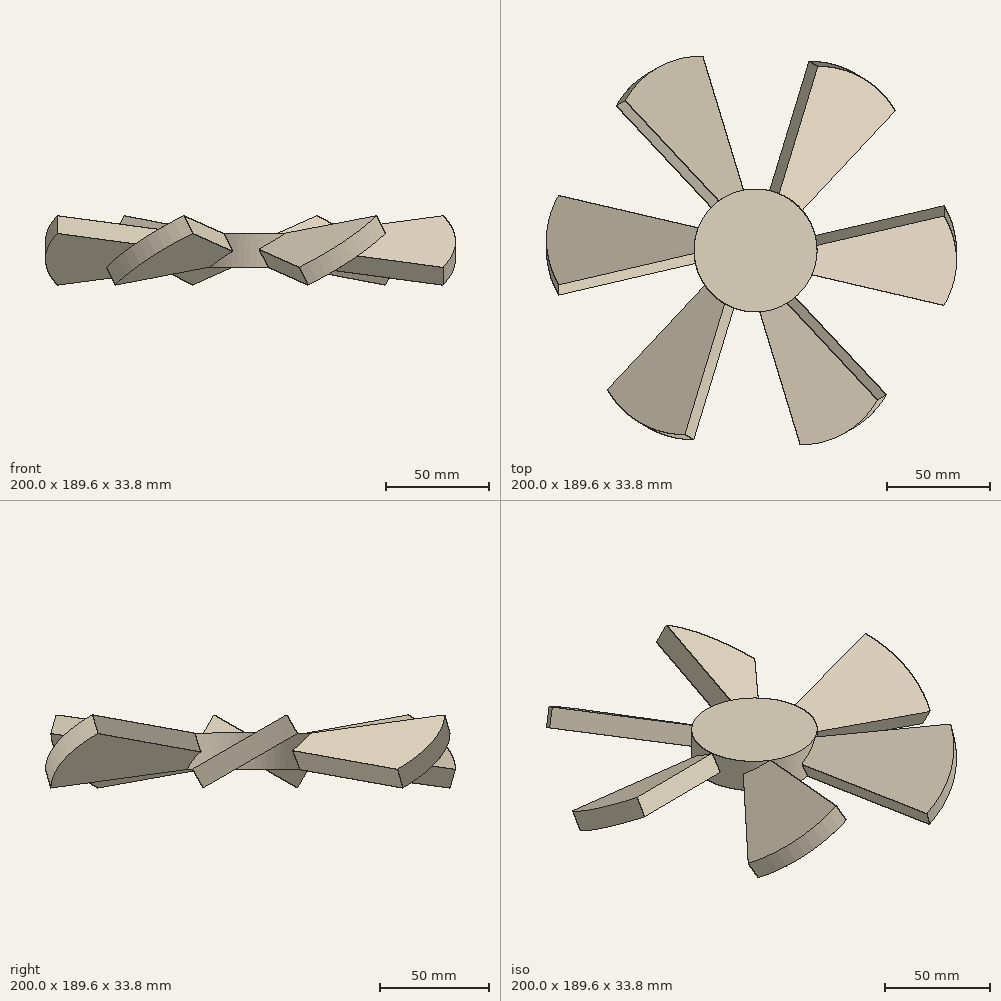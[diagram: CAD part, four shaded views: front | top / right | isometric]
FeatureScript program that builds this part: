
annotation { "Feature Type Name" : "Feature", "Feature Type Description" : "" }
export const myFeature = defineFeature(function(context is Context, id is Id, definition is map)
    precondition{}
    {
        {
            var Q0;
            Q0=qCreatedBy(makeId("Top.planeOp"),FACE);
            var sketch = newSketch(context, id + "F0", { "sketchPlane" : qUnion([Q0])});
            skLineSegment(sketch, "E0", {"start": v(0, 0) * mm, "end": v(94, 25.19) * mm});
            skLineSegment(sketch, "E1", {"start": v(0, 0) * mm, "end": v(94, -25.19) * mm});
            skArc(sketch, "E2", {"start": v(94, -25.19) * mm, "mid": v(100, 0) * mm, "end": v(94, 25.19) * mm});
            skSolve(sketch);
        }
        {
            var Q0;
            Q0=makeQuery(id+"F0.imprint","IMPRINT",FACE,{"disambiguationData":[TD([[makeQuery(id+"F0.imprint","IMPRINT",EDGE,{"derivedFrom":sQuery(id+"F0.wireOp",EDGE,"E0")}),-1.0]])]});
            extrude(context, id + "F1", {"entities" : qUnion([Q0]), "depth" : 5 * mm, "hasSecondDirection" : true, "secondDirectionOppositeDirection" : true, "secondDirectionDepth" : 5 * mm});
        }
        {
            var Q0;
            Q0=qCreatedBy(makeId("Right.planeOp"),FACE);
            var sketch = newSketch(context, id + "F2", { "sketchPlane" : qUnion([Q0])});
            skLineSegment(sketch, "E3", {"start": v(0, 0) * mm, "end": v(0, 134.87) * mm, "construction": true});
            skSolve(sketch);
        }
        {
            var Q0;
            Q0=makeQuery(id+"F1.opExtrude","CAP_FACE",FACE,{"disambiguationData":[OSD([sQuery(id+"F0.wireOp",EDGE,"E0"),sQuery(id+"F0.wireOp",EDGE,"E1"),sQuery(id+"F0.wireOp",EDGE,"E2")])],"isStart":true});
            var sketch = newSketch(context, id + "F3", { "sketchPlane" : qUnion([Q0])});
            skLineSegment(sketch, "E4", {"start": v(0, 0) * mm, "end": v(116.46, 0) * mm, "construction": true});
            skSolve(sketch);
        }
        {
            var Q0;
            Q0=makeQuery(id+"F1.opExtrude","SWEPT_BODY",BODY,{"disambiguationData":[OSD([sQuery(id+"F0.wireOp",EDGE,"E0"),sQuery(id+"F0.wireOp",EDGE,"E1"),sQuery(id+"F0.wireOp",EDGE,"E2")])]});
            var Q1;
            Q1=sQuery(id+"F3.wireOp",EDGE,"E4");
            transform(context, id + "F4", {"entities" : qUnion([Q0]), "transformType" : TransformType.ROTATION, "transformAxis" : qUnion([Q1]), "angle" : 30 * degree, "makeCopy" : false});
        }
        {
            var Q0;
            Q0=makeQuery(id+"F1.opExtrude","SWEPT_BODY",BODY,{"disambiguationData":[OSD([sQuery(id+"F0.wireOp",EDGE,"E0"),sQuery(id+"F0.wireOp",EDGE,"E1"),sQuery(id+"F0.wireOp",EDGE,"E2")])]});
            var Q1;
            Q1=sQuery(id+"F2.wireOp",EDGE,"E3");
            circularPattern(context, id + "F5", {"entities" : qUnion([Q0]), "axis" : qUnion([Q1]), "angle" : 360 * degree, "instanceCount" : 6, "equalSpace" : true});
        }
        {
            var Q0;
            Q0=qCreatedBy(makeId("Top.planeOp"),FACE);
            var sketch = newSketch(context, id + "F6", { "sketchPlane" : qUnion([Q0])});
            skCircle(sketch, "E5", {"center": v(2, 0) * mm, "radius": 30 * mm});
            skSolve(sketch);
        }
        {
            var Q0;
            Q0 = qSketchRegion(id + "F6", true);
            extrude(context, id + "F7", {"entities" : qUnion([Q0]), "depth" : 10 * mm, "hasSecondDirection" : true, "secondDirectionOppositeDirection" : true, "secondDirectionDepth" : 10 * mm});
        }
        {
            var Q0;
            Q0=makeQuery(id+"F5.opPattern","COPY",BODY,{"derivedFrom":makeQuery(id+"F1.opExtrude","SWEPT_BODY",BODY,{"disambiguationData":[OSD([sQuery(id+"F0.wireOp",EDGE,"E0"),sQuery(id+"F0.wireOp",EDGE,"E1"),sQuery(id+"F0.wireOp",EDGE,"E2")])]}),"instanceName":"3"});
            var Q1;
            Q1=makeQuery(id+"F5.opPattern","COPY",BODY,{"derivedFrom":makeQuery(id+"F1.opExtrude","SWEPT_BODY",BODY,{"disambiguationData":[OSD([sQuery(id+"F0.wireOp",EDGE,"E0"),sQuery(id+"F0.wireOp",EDGE,"E1"),sQuery(id+"F0.wireOp",EDGE,"E2")])]}),"instanceName":"2"});
            var Q2;
            Q2=makeQuery(id+"F5.opPattern","COPY",BODY,{"derivedFrom":makeQuery(id+"F1.opExtrude","SWEPT_BODY",BODY,{"disambiguationData":[OSD([sQuery(id+"F0.wireOp",EDGE,"E0"),sQuery(id+"F0.wireOp",EDGE,"E1"),sQuery(id+"F0.wireOp",EDGE,"E2")])]}),"instanceName":"1"});
            var Q3;
            Q3=makeQuery(id+"F1.opExtrude","SWEPT_BODY",BODY,{"disambiguationData":[OSD([sQuery(id+"F0.wireOp",EDGE,"E0"),sQuery(id+"F0.wireOp",EDGE,"E1"),sQuery(id+"F0.wireOp",EDGE,"E2")])]});
            var Q4;
            Q4=makeQuery(id+"F5.opPattern","COPY",BODY,{"derivedFrom":makeQuery(id+"F1.opExtrude","SWEPT_BODY",BODY,{"disambiguationData":[OSD([sQuery(id+"F0.wireOp",EDGE,"E0"),sQuery(id+"F0.wireOp",EDGE,"E1"),sQuery(id+"F0.wireOp",EDGE,"E2")])]}),"instanceName":"5"});
            var Q5;
            Q5=makeQuery(id+"F5.opPattern","COPY",BODY,{"derivedFrom":makeQuery(id+"F1.opExtrude","SWEPT_BODY",BODY,{"disambiguationData":[OSD([sQuery(id+"F0.wireOp",EDGE,"E0"),sQuery(id+"F0.wireOp",EDGE,"E1"),sQuery(id+"F0.wireOp",EDGE,"E2")])]}),"instanceName":"4"});
            var Q6;
            Q6=makeQuery(id+"F7.opExtrude","SWEPT_BODY",BODY,{"disambiguationData":[OSD([sQuery(id+"F6.wireOp",EDGE,"E5")])]});
            booleanBodies(context, id + "F8", {"operationType" : BooleanOperationType.UNION, "tools" : qUnion([Q0, Q1, Q2, Q3, Q4, Q5, Q6])});
        }
        {
            var Q0;
            {var subQ0=sQuery(id+"F0.wireOp",EDGE,"E0");Q0=makeQuery(id+"F8.opBoolean","INTERSECT",VERTEX,{"derivedFrom":[makeQuery(id+"F5.opPattern","COPY",FACE,{"derivedFrom":makeQuery(id+"F1.opExtrude","SWEPT_FACE",FACE,{"disambiguationData":[OSD([subQ0])]}),"instanceName":"4"}),makeQuery(id+"F5.opPattern","COPY",FACE,{"derivedFrom":makeQuery(id+"F1.opExtrude","CAP_FACE",FACE,{"disambiguationData":[OSD([subQ0,sQuery(id+"F0.wireOp",EDGE,"E1"),sQuery(id+"F0.wireOp",EDGE,"E2")])],"isStart":false}),"instanceName":"4"}),makeQuery(id+"F7.opExtrude","SWEPT_FACE",FACE,{"disambiguationData":[OSD([sQuery(id+"F6.wireOp",EDGE,"E5")])]})]});}
            var Q1;
            {var subQ0=sQuery(id+"F0.wireOp",EDGE,"E0");Q1=makeQuery(id+"F8.opBoolean","INTERSECT",VERTEX,{"derivedFrom":[makeQuery(id+"F1.opExtrude","SWEPT_FACE",FACE,{"disambiguationData":[OSD([subQ0])]}),makeQuery(id+"F1.opExtrude","CAP_FACE",FACE,{"disambiguationData":[OSD([subQ0,sQuery(id+"F0.wireOp",EDGE,"E1"),sQuery(id+"F0.wireOp",EDGE,"E2")])],"isStart":false}),makeQuery(id+"F7.opExtrude","SWEPT_FACE",FACE,{"disambiguationData":[OSD([sQuery(id+"F6.wireOp",EDGE,"E5")])]})]});}
            var Q2;
            {var subQ0=sQuery(id+"F0.wireOp",EDGE,"E0");Q2=makeQuery(id+"F8.opBoolean","INTERSECT",VERTEX,{"derivedFrom":[makeQuery(id+"F5.opPattern","COPY",FACE,{"derivedFrom":makeQuery(id+"F1.opExtrude","SWEPT_FACE",FACE,{"disambiguationData":[OSD([subQ0])]}),"instanceName":"2"}),makeQuery(id+"F5.opPattern","COPY",FACE,{"derivedFrom":makeQuery(id+"F1.opExtrude","CAP_FACE",FACE,{"disambiguationData":[OSD([subQ0,sQuery(id+"F0.wireOp",EDGE,"E1"),sQuery(id+"F0.wireOp",EDGE,"E2")])],"isStart":false}),"instanceName":"2"}),makeQuery(id+"F7.opExtrude","SWEPT_FACE",FACE,{"disambiguationData":[OSD([sQuery(id+"F6.wireOp",EDGE,"E5")])]})]});}
            cPlane(context, id + "F9", {"entities" : qUnion([Q0, Q1, Q2]), "cplaneType" : CPlaneType.THREE_POINT, "offset" : 25 * mm, "width" : 150 * mm, "height" : 150 * mm});
        }
        {
            var Q0;
            Q0=makeQuery(id+"F7.opExtrude","CAP_FACE",FACE,{"disambiguationData":[OSD([sQuery(id+"F6.wireOp",EDGE,"E5")])],"isStart":false});
            var Q1;
            Q1=qCreatedBy(id+"F9.planeOp",FACE);
            extrude(context, id + "F10", {"entities" : qUnion([Q0]), "operationType" : NewBodyOperationType.REMOVE, "endBound" : BoundingType.UP_TO_SURFACE, "oppositeDirection" : true, "endBoundEntityFace" : qUnion([Q1]), "depth" : 25 * mm});
        }
        {
            var Q0;
            {var subQ0=sQuery(id+"F0.wireOp",EDGE,"E1");Q0=makeQuery(id+"F8.opBoolean","INTERSECT",VERTEX,{"derivedFrom":[makeQuery(id+"F1.opExtrude","CAP_FACE",FACE,{"disambiguationData":[OSD([sQuery(id+"F0.wireOp",EDGE,"E0"),subQ0,sQuery(id+"F0.wireOp",EDGE,"E2")])],"isStart":true}),makeQuery(id+"F1.opExtrude","SWEPT_FACE",FACE,{"disambiguationData":[OSD([subQ0])]}),makeQuery(id+"F7.opExtrude","SWEPT_FACE",FACE,{"disambiguationData":[OSD([sQuery(id+"F6.wireOp",EDGE,"E5")])]})]});}
            var Q1;
            {var subQ0=sQuery(id+"F0.wireOp",EDGE,"E1");Q1=makeQuery(id+"F8.opBoolean","INTERSECT",VERTEX,{"derivedFrom":[makeQuery(id+"F5.opPattern","COPY",FACE,{"derivedFrom":makeQuery(id+"F1.opExtrude","CAP_FACE",FACE,{"disambiguationData":[OSD([sQuery(id+"F0.wireOp",EDGE,"E0"),subQ0,sQuery(id+"F0.wireOp",EDGE,"E2")])],"isStart":true}),"instanceName":"1"}),makeQuery(id+"F5.opPattern","COPY",FACE,{"derivedFrom":makeQuery(id+"F1.opExtrude","SWEPT_FACE",FACE,{"disambiguationData":[OSD([subQ0])]}),"instanceName":"1"}),makeQuery(id+"F7.opExtrude","SWEPT_FACE",FACE,{"disambiguationData":[OSD([sQuery(id+"F6.wireOp",EDGE,"E5")])]})]});}
            var Q2;
            {var subQ0=sQuery(id+"F0.wireOp",EDGE,"E1");Q2=makeQuery(id+"F8.opBoolean","INTERSECT",VERTEX,{"derivedFrom":[makeQuery(id+"F5.opPattern","COPY",FACE,{"derivedFrom":makeQuery(id+"F1.opExtrude","CAP_FACE",FACE,{"disambiguationData":[OSD([sQuery(id+"F0.wireOp",EDGE,"E0"),subQ0,sQuery(id+"F0.wireOp",EDGE,"E2")])],"isStart":true}),"instanceName":"3"}),makeQuery(id+"F5.opPattern","COPY",FACE,{"derivedFrom":makeQuery(id+"F1.opExtrude","SWEPT_FACE",FACE,{"disambiguationData":[OSD([subQ0])]}),"instanceName":"3"}),makeQuery(id+"F7.opExtrude","SWEPT_FACE",FACE,{"disambiguationData":[OSD([sQuery(id+"F6.wireOp",EDGE,"E5")])]})]});}
            cPlane(context, id + "F11", {"entities" : qUnion([Q0, Q1, Q2]), "cplaneType" : CPlaneType.THREE_POINT, "offset" : 25 * mm, "width" : 150 * mm, "height" : 150 * mm});
        }
        {
            var Q0;
            Q0=makeQuery(id+"F7.opExtrude","CAP_FACE",FACE,{"disambiguationData":[OSD([sQuery(id+"F6.wireOp",EDGE,"E5")])],"isStart":true});
            var Q1;
            Q1=qCreatedBy(id+"F11.planeOp",FACE);
            extrude(context, id + "F12", {"entities" : qUnion([Q0]), "operationType" : NewBodyOperationType.REMOVE, "endBound" : BoundingType.UP_TO_SURFACE, "oppositeDirection" : true, "endBoundEntityFace" : qUnion([Q1]), "depth" : 25 * mm});
        }
    });
